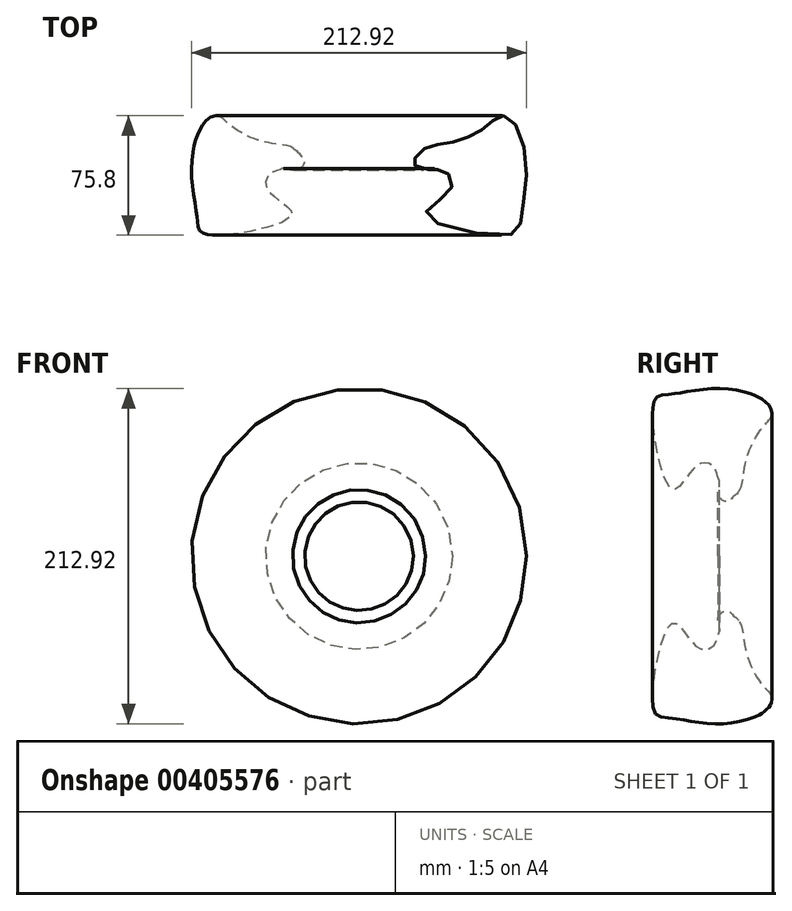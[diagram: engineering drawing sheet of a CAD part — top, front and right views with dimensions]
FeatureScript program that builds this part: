
annotation { "Feature Type Name" : "Feature", "Feature Type Description" : "" }
export const myFeature = defineFeature(function(context is Context, id is Id, definition is map)
    precondition{}
    {
        {
            var Q0;
            Q0=qCreatedBy(makeId("Top.planeOp"),FACE);
            var sketch = newSketch(context, id + "F0", { "sketchPlane" : qUnion([Q0])});
            skFitSpline(sketch, "E0", {"points": [v(3.43, 24.22) * mm, v(12.48, 26.67) * mm, v(24.71, 29.12) * mm, v(35.97, 33.77) * mm, v(45.02, 40.13) * mm, v(51.38, 44.78) * mm, v(59.46, 41.35) * mm, v(68.27, 12.72) * mm, v(64.6, -20.55) * mm, v(59.7, -30.1) * mm, v(4.9, -19.33) * mm, v(9.05, -11.5) * mm, v(20.8, 0) * mm, v(18.1, 8.32) * mm, v(11.74, 10.77) * mm, v(9.79, 11.5) * mm, v(0, 11.01) * mm, v(-3.67, 16.4) * mm, v(-2.94, 17.62) * mm, v(3.43, 24.22) * mm]});
            skPoint(sketch, "E1.center.orphan", {"position": v(-7.83, 0) * mm});
            skLineSegment(sketch, "E2", {"start": v(-38.17, 44.29) * mm, "end": v(-38.17, -28.14) * mm});
            skSolve(sketch);
        }
        {
            var Q0;
            Q0=makeQuery(id+"F0.imprint","IMPRINT",FACE,{"disambiguationData":[TD([[makeQuery(id+"F0.imprint","IMPRINT",EDGE,{"derivedFrom":sQuery(id+"F0.wireOp",EDGE,"E0")}),-1.0]])]});
            var Q1;
            Q1=sQuery(id+"F0.wireOp",EDGE,"E2");
            revolve(context, id + "F1", {"entities" : qUnion([Q0]), "axis" : qUnion([Q1]), "revolveType" : RevolveType.FULL});
        }
    });
